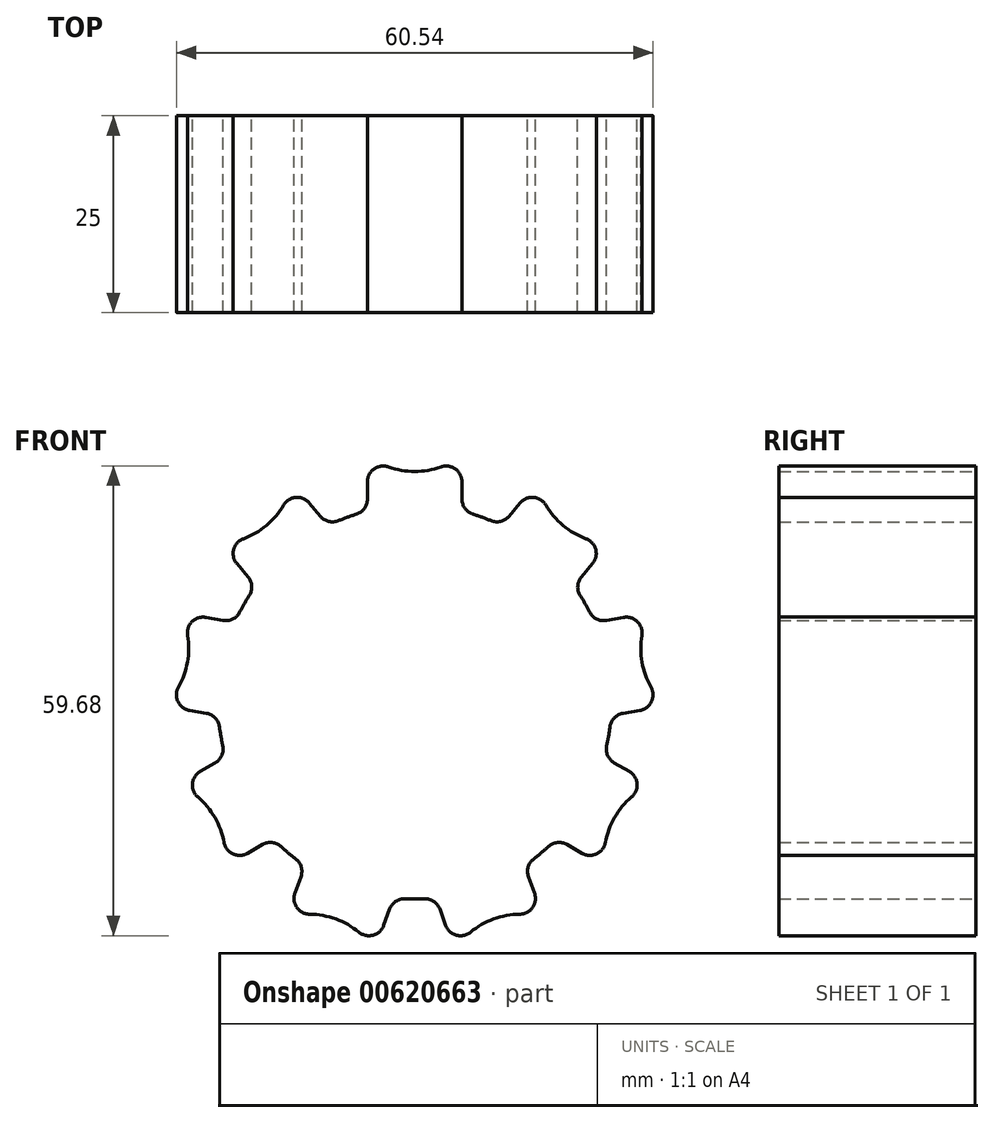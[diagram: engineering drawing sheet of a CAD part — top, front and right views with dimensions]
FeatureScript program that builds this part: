
annotation { "Feature Type Name" : "Feature", "Feature Type Description" : "" }
export const myFeature = defineFeature(function(context is Context, id is Id, definition is map)
    precondition{}
    {
        {
            var Q0;
            Q0=qCreatedBy(makeId("Front.planeOp"),FACE);
            var sketch = newSketch(context, id + "F0", { "sketchPlane" : qUnion([Q0])});
            skCircle(sketch, "E0", {"center": v(0, 0) * mm, "radius": 25 * mm});
            skLineSegment(sketch, "E1", {"start": v(0, 0) * mm, "end": v(0, 46.96) * mm, "construction": true});
            skLineSegment(sketch, "E2", {"start": v(-6, 24.27) * mm, "end": v(-6, 28) * mm});
            skArc(sketch, "E3", {"start": v(-3.33, 29.89) * mm, "mid": v(0, 29.31) * mm, "end": v(3.33, 29.89) * mm});
            skArc(sketch, "E4", {"start": v(-3.33, 29.89) * mm, "mid": v(-5.15, 29.63) * mm, "end": v(-6, 28) * mm});
            skLineSegment(sketch, "E5.MirrorCS", {"start": v(6, 24.27) * mm, "end": v(6, 28) * mm});
            skArc(sketch, "E6.MirrorC", {"start": v(3.33, 29.89) * mm, "mid": v(5.15, 29.63) * mm, "end": v(6, 28) * mm});
            skSolve(sketch);
        }
        {
            var Q0;
            Q0 = qSketchRegion(id + "F0", true);
            extrude(context, id + "F1", {"entities" : qUnion([Q0]), "depth" : 25 * mm, "offsetDistance" : 25 * mm});
        }
        {
            var Q0;
            Q0=makeQuery(id+"F1.opExtrude","SWEPT_EDGE",EDGE,{"disambiguationData":[OSD([sQuery(id+"F0.wireOp",EDGE,"E0"),sQuery(id+"F0.wireOp",EDGE,"E2")])]});
            var Q1;
            Q1=makeQuery(id+"F1.opExtrude","SWEPT_EDGE",EDGE,{"disambiguationData":[OSD([sQuery(id+"F0.wireOp",EDGE,"E0"),sQuery(id+"F0.wireOp",EDGE,"E5.MirrorCS")])]});
            fillet(context, id + "F2", {"entities" : qUnion([Q0, Q1]), "radius" : 2 * mm, "tangentPropagation" : true, "allowEdgeOverflow" : false});
        }
        {
            var Q0;
            Q0=qCreatedBy(makeId("Right.planeOp"),FACE);
            var sketch = newSketch(context, id + "F3", { "sketchPlane" : qUnion([Q0])});
            skLineSegment(sketch, "E7", {"start": v(0, 0) * mm, "end": v(-28.13, 0) * mm, "construction": true});
            skSolve(sketch);
        }
        {
            var Q0;
            Q0=makeQuery(id+"F1.opExtrude","SWEPT_BODY",BODY,{"disambiguationData":[OSD([sQuery(id+"F0.wireOp",EDGE,"E0"),sQuery(id+"F0.wireOp",EDGE,"E2"),sQuery(id+"F0.wireOp",EDGE,"E3"),sQuery(id+"F0.wireOp",EDGE,"E4"),sQuery(id+"F0.wireOp",EDGE,"E5.MirrorCS"),sQuery(id+"F0.wireOp",EDGE,"E6.MirrorC")])]});
            var Q1;
            Q1=sQuery(id+"F3.wireOp",EDGE,"E7");
            circularPattern(context, id + "F4", {"operationType" : NewBodyOperationType.ADD, "entities" : qUnion([Q0]), "axis" : qUnion([Q1]), "angle" : 360 * degree, "instanceCount" : 9, "equalSpace" : true});
        }
    });
